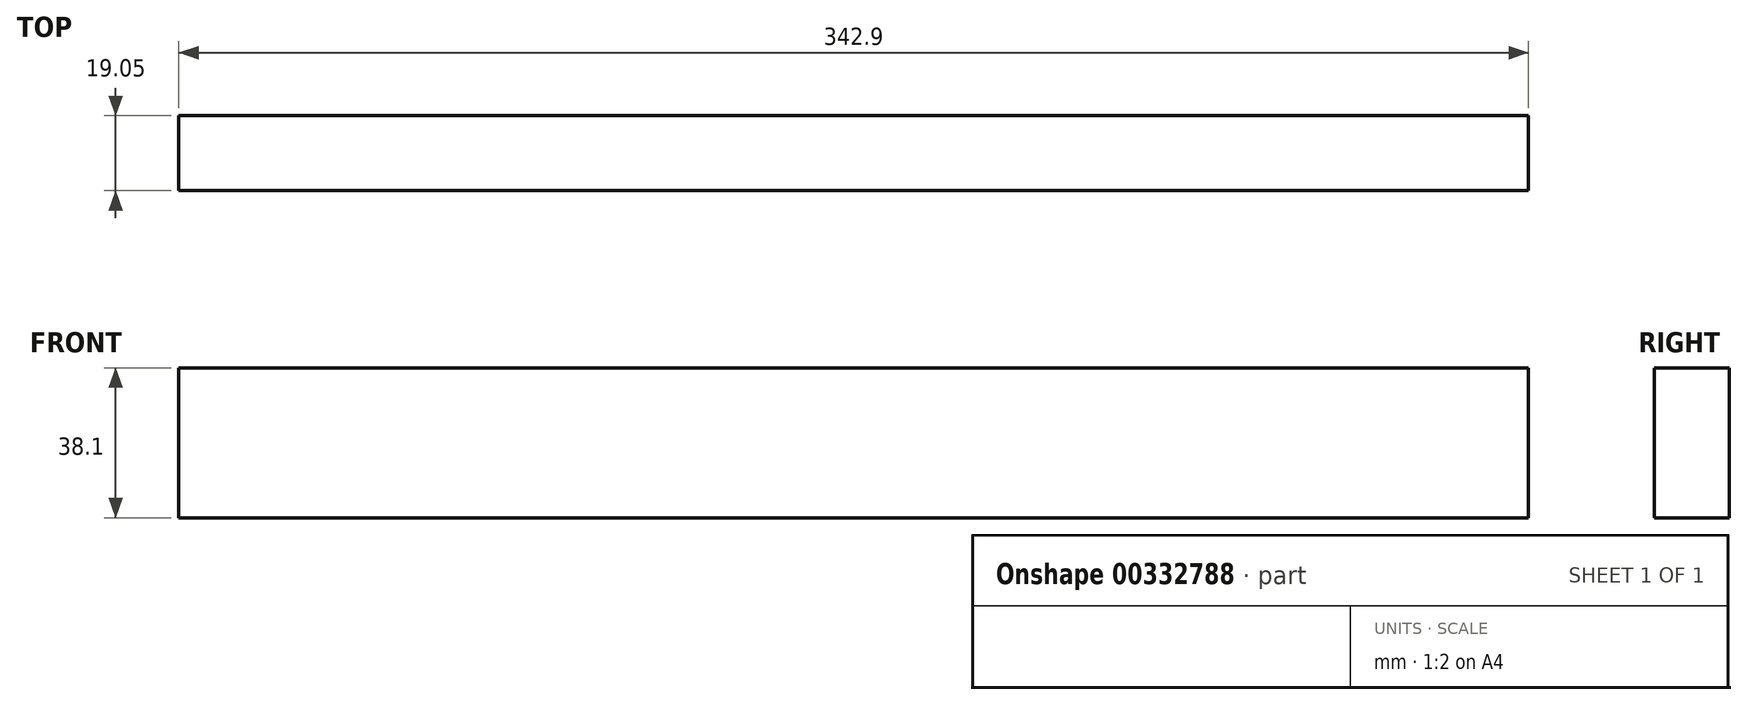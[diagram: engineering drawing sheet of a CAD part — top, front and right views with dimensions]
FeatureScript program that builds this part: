
annotation { "Feature Type Name" : "Feature", "Feature Type Description" : "" }
export const myFeature = defineFeature(function(context is Context, id is Id, definition is map)
    precondition{}
    {
        {
            var Q0;
            Q0=qCreatedBy(makeId("Front.planeOp"),FACE);
            var sketch = newSketch(context, id + "F0", { "sketchPlane" : qUnion([Q0])});
            skLineSegment(sketch, "E0.bottom", {"start": v(171.45, 19.05) * mm, "end": v(-171.45, 19.05) * mm});
            skLineSegment(sketch, "E0.top", {"start": v(171.45, -19.05) * mm, "end": v(-171.45, -19.05) * mm});
            skLineSegment(sketch, "E0.left", {"start": v(171.45, 19.05) * mm, "end": v(171.45, -19.05) * mm});
            skLineSegment(sketch, "E0.right", {"start": v(-171.45, 19.05) * mm, "end": v(-171.45, -19.05) * mm});
            skPoint(sketch, "E0.middle", {"position": v(0, 0) * mm});
            skSolve(sketch);
        }
        {
            var Q0;
            Q0 = qSketchRegion(id + "F0", true);
            extrude(context, id + "F1", {"entities" : qUnion([Q0]), "depth" : 19.05 * mm});
        }
    });
